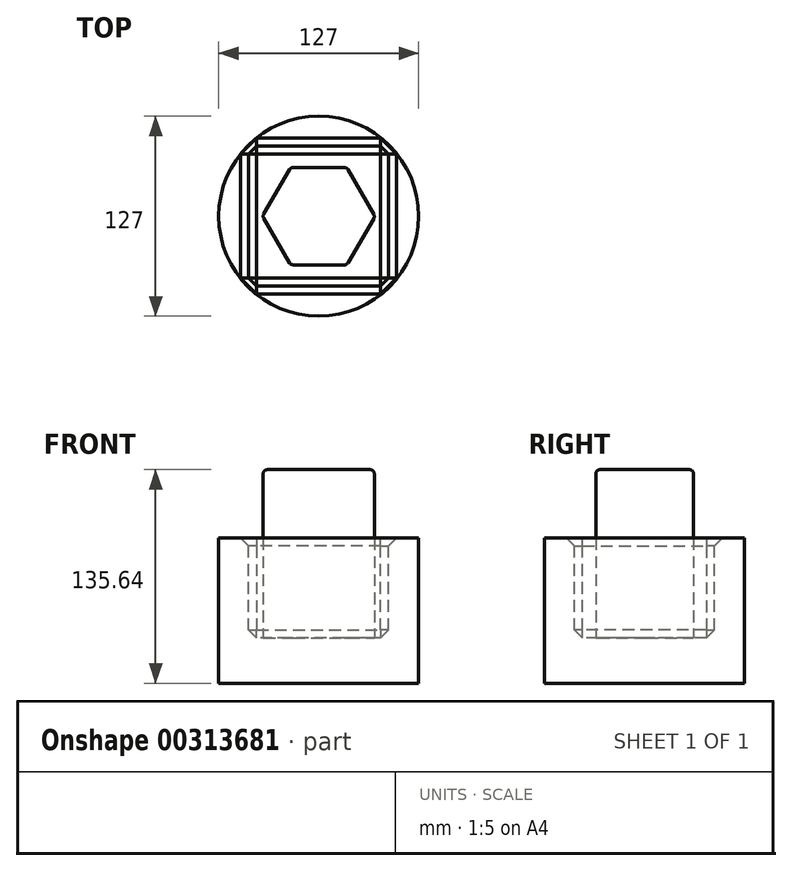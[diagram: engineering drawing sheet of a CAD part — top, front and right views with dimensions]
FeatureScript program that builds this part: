
annotation { "Feature Type Name" : "Feature", "Feature Type Description" : "" }
export const myFeature = defineFeature(function(context is Context, id is Id, definition is map)
    precondition{}
    {
        {
            var Q0;
            Q0=qCreatedBy(makeId("Top.planeOp"),FACE);
            var sketch = newSketch(context, id + "F0", { "sketchPlane" : qUnion([Q0])});
            skCircle(sketch, "E0", {"center": v(0, 0) * mm, "radius": 63.5 * mm});
            skSolve(sketch);
        }
        {
            var Q0;
            Q0=makeQuery(id+"F0.imprint","IMPRINT",FACE,{"disambiguationData":[TD([[makeQuery(id+"F0.imprint","IMPRINT",EDGE,{"derivedFrom":sQuery(id+"F0.wireOp",EDGE,"E0")}),1.0]])]});
            extrude(context, id + "F1", {"entities" : qUnion([Q0]), "depth" : 92.2 * mm});
        }
        {
            var Q0;
            Q0=makeQuery(id+"F1.opExtrude","CAP_FACE",FACE,{"disambiguationData":[OSD([sQuery(id+"F0.wireOp",EDGE,"E0")])],"isStart":false});
            var sketch = newSketch(context, id + "F2", { "sketchPlane" : qUnion([Q0])});
            skLineSegment(sketch, "E1.bottom", {"start": v(44.45, 44.45) * mm, "end": v(-44.45, 44.45) * mm});
            skLineSegment(sketch, "E1.top", {"start": v(44.45, -44.45) * mm, "end": v(-44.45, -44.45) * mm});
            skLineSegment(sketch, "E1.left", {"start": v(44.45, 44.45) * mm, "end": v(44.45, -44.45) * mm});
            skLineSegment(sketch, "E1.right", {"start": v(-44.45, 44.45) * mm, "end": v(-44.45, -44.45) * mm});
            skPoint(sketch, "E1.middle", {"position": v(0, 0) * mm});
            skSolve(sketch);
        }
        {
            var Q0;
            Q0=makeQuery(id+"F2.imprint","IMPRINT",FACE,{"disambiguationData":[TD([[makeQuery(id+"F2.imprint","IMPRINT",EDGE,{"derivedFrom":sQuery(id+"F2.wireOp",EDGE,"E1.bottom")}),1.0]])]});
            extrude(context, id + "F3", {"entities" : qUnion([Q0]), "operationType" : NewBodyOperationType.REMOVE, "oppositeDirection" : true, "depth" : 63.5 * mm});
        }
        {
            var Q0;
            Q0=makeQuery(id+"F3.boolean.opBoolean","COPY",FACE,{"derivedFrom":makeQuery(id+"F3.opExtrude","CAP_FACE",FACE,{"disambiguationData":[OSD([sQuery(id+"F2.wireOp",EDGE,"E1.bottom"),sQuery(id+"F2.wireOp",EDGE,"E1.top"),sQuery(id+"F2.wireOp",EDGE,"E1.left"),sQuery(id+"F2.wireOp",EDGE,"E1.right")])],"isStart":false})});
            var sketch = newSketch(context, id + "F4", { "sketchPlane" : qUnion([Q0])});
            skCircle(sketch, "E2.cCircle", {"center": v(0, 0) * mm, "radius": 30.9 * mm, "construction": true});
            skLineSegment(sketch, "E2.0", {"start": v(17.93, 30.85) * mm, "end": v(35.68, -0.1) * mm});
            skLineSegment(sketch, "E2.1", {"start": v(35.68, -0.1) * mm, "end": v(17.75, -30.95) * mm});
            skLineSegment(sketch, "E2.2", {"start": v(17.75, -30.95) * mm, "end": v(-17.93, -30.85) * mm});
            skLineSegment(sketch, "E2.3", {"start": v(-17.93, -30.85) * mm, "end": v(-35.68, 0.1) * mm});
            skLineSegment(sketch, "E2.4", {"start": v(-35.68, 0.1) * mm, "end": v(-17.75, 30.95) * mm});
            skLineSegment(sketch, "E2.5", {"start": v(-17.75, 30.95) * mm, "end": v(17.93, 30.85) * mm});
            skPoint(sketch, "E2.0.midPoint", {"position": v(26.8, 15.37) * mm});
            skSolve(sketch);
        }
        {
            var Q0;
            Q0=makeQuery(id+"F4.imprint","IMPRINT",FACE,{"disambiguationData":[TD([[makeQuery(id+"F4.imprint","IMPRINT",EDGE,{"derivedFrom":sQuery(id+"F4.wireOp",EDGE,"E2.0")}),-1.0]])]});
            extrude(context, id + "F5", {"entities" : qUnion([Q0]), "operationType" : NewBodyOperationType.ADD, "depth" : 106.93 * mm});
        }
        {
            var Q0;
            Q0=makeQuery(id+"F5.opExtrude","SWEPT_EDGE",EDGE,{"disambiguationData":[OSD([sQuery(id+"F4.wireOp",EDGE,"E2.3"),sQuery(id+"F4.wireOp",EDGE,"E2.4")])]});
            var Q1;
            Q1=makeQuery(id+"F5.opExtrude","SWEPT_EDGE",EDGE,{"disambiguationData":[OSD([sQuery(id+"F4.wireOp",EDGE,"E2.2"),sQuery(id+"F4.wireOp",EDGE,"E2.3")])]});
            var Q2;
            Q2=makeQuery(id+"F5.opExtrude","SWEPT_EDGE",EDGE,{"disambiguationData":[OSD([sQuery(id+"F4.wireOp",EDGE,"E2.1"),sQuery(id+"F4.wireOp",EDGE,"E2.2")])]});
            var Q3;
            Q3=makeQuery(id+"F5.opExtrude","SWEPT_EDGE",EDGE,{"disambiguationData":[OSD([sQuery(id+"F4.wireOp",EDGE,"E2.4"),sQuery(id+"F4.wireOp",EDGE,"E2.5")])]});
            var Q4;
            Q4=makeQuery(id+"F3.boolean.opBoolean","COPY",EDGE,{"derivedFrom":makeQuery(id+"F3.opExtrude","CAP_EDGE",EDGE,{"disambiguationData":[OSD([sQuery(id+"F2.wireOp",EDGE,"E1.right")])],"isStart":true})});
            var Q5;
            Q5=makeQuery(id+"F3.boolean.opBoolean","COPY",EDGE,{"derivedFrom":makeQuery(id+"F3.opExtrude","CAP_EDGE",EDGE,{"disambiguationData":[OSD([sQuery(id+"F2.wireOp",EDGE,"E1.bottom")])],"isStart":true})});
            var Q6;
            Q6=makeQuery(id+"F3.boolean.opBoolean","COPY",EDGE,{"derivedFrom":makeQuery(id+"F3.opExtrude","CAP_EDGE",EDGE,{"disambiguationData":[OSD([sQuery(id+"F2.wireOp",EDGE,"E1.top")])],"isStart":true})});
            var Q7;
            Q7=makeQuery(id+"F3.boolean.opBoolean","COPY",EDGE,{"derivedFrom":makeQuery(id+"F3.opExtrude","CAP_EDGE",EDGE,{"disambiguationData":[OSD([sQuery(id+"F2.wireOp",EDGE,"E1.left")])],"isStart":true})});
            var Q8;
            Q8=makeQuery(id+"F5.opExtrude","SWEPT_EDGE",EDGE,{"disambiguationData":[OSD([sQuery(id+"F4.wireOp",EDGE,"E2.0"),sQuery(id+"F4.wireOp",EDGE,"E2.5")])]});
            var Q9;
            Q9=makeQuery(id+"F5.opExtrude","SWEPT_EDGE",EDGE,{"disambiguationData":[OSD([sQuery(id+"F4.wireOp",EDGE,"E2.0"),sQuery(id+"F4.wireOp",EDGE,"E2.1")])]});
            fillet(context, id + "F6", {"entities" : qUnion([Q0, Q1, Q2, Q3, Q4, Q5, Q6, Q7, Q8, Q9]), "radius" : 2.54 * mm, "tangentPropagation" : true, "allowEdgeOverflow" : false});
        }
        {
            var Q0;
            Q0=makeQuery(id+"F5.opExtrude","CAP_EDGE",EDGE,{"disambiguationData":[OSD([sQuery(id+"F4.wireOp",EDGE,"E2.4")])],"isStart":false});
            var Q1;
            Q1=makeQuery(id+"F5.opExtrude","CAP_EDGE",EDGE,{"disambiguationData":[OSD([sQuery(id+"F4.wireOp",EDGE,"E2.5")])],"isStart":false});
            fillet(context, id + "F7", {"entities" : qUnion([Q0, Q1]), "radius" : 2.54 * mm, "tangentPropagation" : true, "allowEdgeOverflow" : false});
        }
        {
            var Q0;
            Q0=makeQuery(id+"F3.boolean.opBoolean","COPY",FACE,{"derivedFrom":makeQuery(id+"F3.opExtrude","SWEPT_FACE",FACE,{"disambiguationData":[OSD([sQuery(id+"F2.wireOp",EDGE,"E1.left")])]})});
            var Q1;
            Q1=makeQuery(id+"F3.boolean.opBoolean","COPY",FACE,{"derivedFrom":makeQuery(id+"F3.opExtrude","SWEPT_FACE",FACE,{"disambiguationData":[OSD([sQuery(id+"F2.wireOp",EDGE,"E1.top")])]})});
            var Q2;
            Q2=makeQuery(id+"F6.opFillet","BLEND_EDGE",EDGE,{"blendedFrom":[makeQuery(id+"F3.boolean.opBoolean","COPY",EDGE,{"derivedFrom":makeQuery(id+"F3.opExtrude","CAP_EDGE",EDGE,{"disambiguationData":[OSD([sQuery(id+"F2.wireOp",EDGE,"E1.right")])],"isStart":true})}),makeQuery(id+"F1.opExtrude","CAP_FACE",FACE,{"disambiguationData":[OSD([sQuery(id+"F0.wireOp",EDGE,"E0")])],"isStart":false})],"blendedInto":[makeQuery(id+"F1.opExtrude","CAP_FACE",FACE,{"disambiguationData":[OSD([sQuery(id+"F0.wireOp",EDGE,"E0")])],"isStart":false})]});
            var Q3;
            Q3=makeQuery(id+"F6.opFillet","BLEND_EDGE",EDGE,{"blendedFrom":[makeQuery(id+"F3.boolean.opBoolean","COPY",EDGE,{"derivedFrom":makeQuery(id+"F3.opExtrude","CAP_EDGE",EDGE,{"disambiguationData":[OSD([sQuery(id+"F2.wireOp",EDGE,"E1.bottom")])],"isStart":true})}),makeQuery(id+"F1.opExtrude","CAP_FACE",FACE,{"disambiguationData":[OSD([sQuery(id+"F0.wireOp",EDGE,"E0")])],"isStart":false})],"blendedInto":[makeQuery(id+"F1.opExtrude","CAP_FACE",FACE,{"disambiguationData":[OSD([sQuery(id+"F0.wireOp",EDGE,"E0")])],"isStart":false})]});
            var Q4;
            Q4=makeQuery(id+"F3.boolean.opBoolean","COPY",FACE,{"derivedFrom":makeQuery(id+"F3.opExtrude","SWEPT_FACE",FACE,{"disambiguationData":[OSD([sQuery(id+"F2.wireOp",EDGE,"E1.right")])]})});
            var Q5;
            Q5=makeQuery(id+"F3.boolean.opBoolean","COPY",FACE,{"derivedFrom":makeQuery(id+"F3.opExtrude","SWEPT_FACE",FACE,{"disambiguationData":[OSD([sQuery(id+"F2.wireOp",EDGE,"E1.bottom")])]})});
            chamfer(context, id + "F8", {"entities" : qUnion([Q0, Q1, Q2, Q3, Q4, Q5]), "width" : 5.08 * mm, "tangentPropagation" : true});
        }
    });
